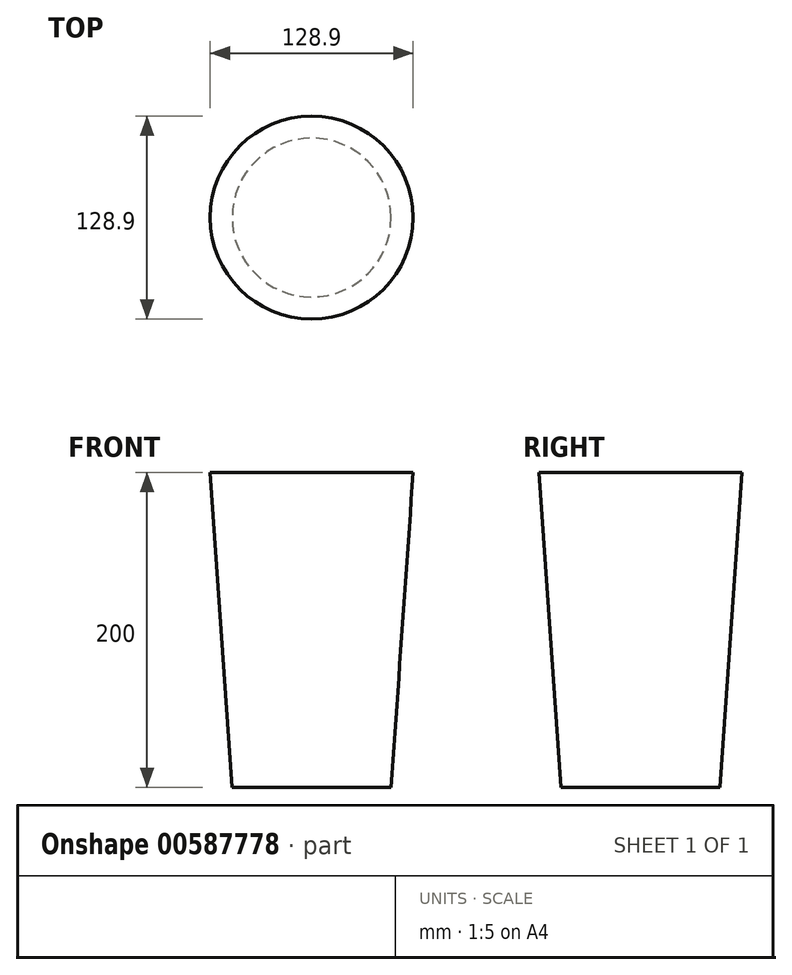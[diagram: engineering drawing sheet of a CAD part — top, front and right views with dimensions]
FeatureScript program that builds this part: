
annotation { "Feature Type Name" : "Feature", "Feature Type Description" : "" }
export const myFeature = defineFeature(function(context is Context, id is Id, definition is map)
    precondition{}
    {
        {
            var Q0;
            Q0=qCreatedBy(makeId("Top.planeOp"),FACE);
            var sketch = newSketch(context, id + "F0", { "sketchPlane" : qUnion([Q0])});
            skCircle(sketch, "E0", {"center": v(0, 0) * mm, "radius": 50.47 * mm});
            skSolve(sketch);
        }
        {
            var Q0;
            Q0=makeQuery(id+"F0.imprint","IMPRINT",FACE,{"disambiguationData":[TD([[makeQuery(id+"F0.imprint","IMPRINT",EDGE,{"derivedFrom":sQuery(id+"F0.wireOp",EDGE,"E0")}),1.0]])]});
            extrude(context, id + "F1", {"entities" : qUnion([Q0]), "depth" : 200 * mm, "offsetDistance" : 25 * mm, "hasDraft" : true, "draftAngle" : 4 * degree});
        }
    });
